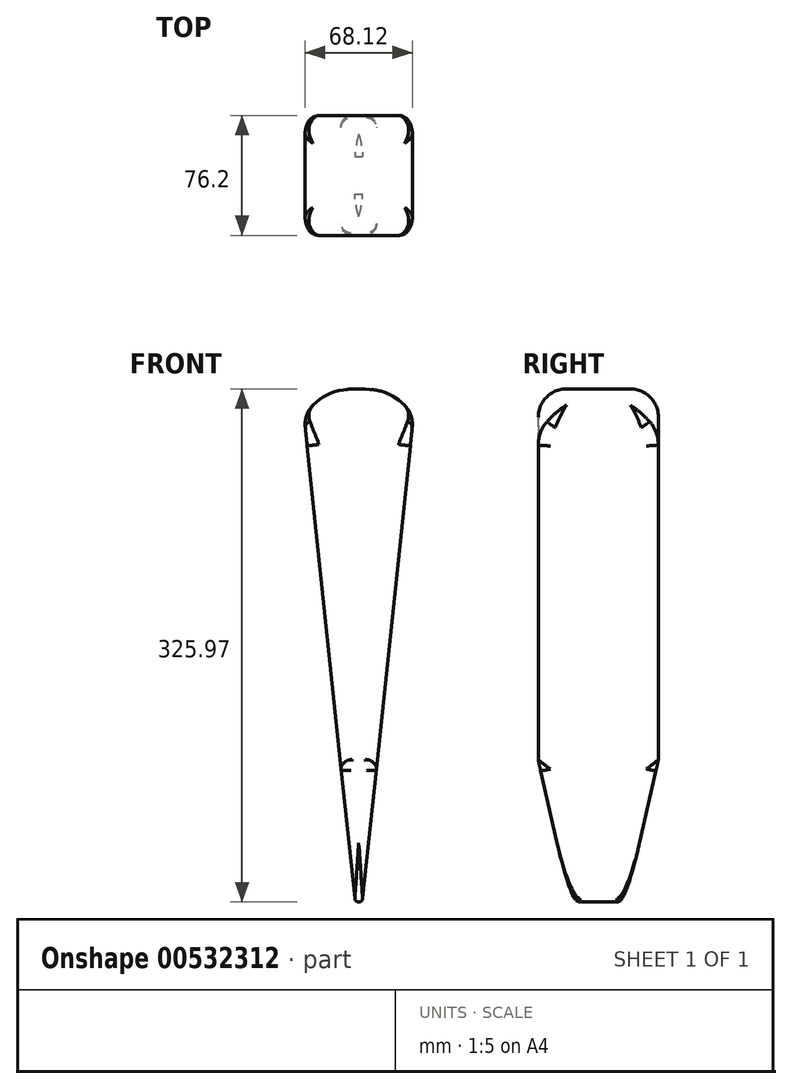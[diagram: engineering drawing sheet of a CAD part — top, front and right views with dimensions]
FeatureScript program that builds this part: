
annotation { "Feature Type Name" : "Feature", "Feature Type Description" : "" }
export const myFeature = defineFeature(function(context is Context, id is Id, definition is map)
    precondition{}
    {
        {
            var Q0;
            Q0=qCreatedBy(makeId("Front.planeOp"),FACE);
            var sketch = newSketch(context, id + "F0", { "sketchPlane" : qUnion([Q0])});
            skLineSegment(sketch, "E0", {"start": v(-58.84, 108.82) * mm, "end": v(-24.13, -221.38) * mm});
            skLineSegment(sketch, "E1", {"start": v(10.58, 108.82) * mm, "end": v(-24.13, -221.38) * mm});
            skLineSegment(sketch, "E2", {"start": v(-58.84, 108.82) * mm, "end": v(10.58, 108.82) * mm, "construction": true});
            skPoint(sketch, "E3", {"position": v(-24.13, 126.34) * mm});
            skFitSpline(sketch, "E4", {"points": [v(-58.84, 108.82) * mm, v(-24.13, 126.34) * mm, v(10.58, 108.82) * mm], "startDerivative": vector(63.45, 96.01) * mm, "endDerivative": vector(63.45, -96.01) * mm});
            skLineSegment(sketch, "E5", {"start": v(-58.84, 108.82) * mm, "end": v(-24.13, 126.34) * mm, "construction": true});
            skLineSegment(sketch, "E6", {"start": v(10.58, 108.82) * mm, "end": v(-24.13, 126.34) * mm, "construction": true});
            skLineSegment(sketch, "E7", {"start": v(-24.13, 126.34) * mm, "end": v(-24.13, 108.82) * mm, "construction": true});
            skLineSegment(sketch, "E8", {"start": v(-48.26, 124.82) * mm, "end": v(0, 124.82) * mm, "construction": true});
            skLineSegment(sketch, "E9", {"start": v(-58.84, 108.82) * mm, "end": v(-48.26, 124.82) * mm, "construction": true});
            skLineSegment(sketch, "E10", {"start": v(0, 124.82) * mm, "end": v(10.58, 108.82) * mm, "construction": true});
            skSolve(sketch);
        }
        {
            var Q0;
            Q0=makeQuery(id+"F0.imprint","IMPRINT",FACE,{"disambiguationData":[TD([[makeQuery(id+"F0.imprint","IMPRINT",EDGE,{"derivedFrom":sQuery(id+"F0.wireOp",EDGE,"E0")}),1.0]])]});
            extrude(context, id + "F1", {"entities" : qUnion([Q0]), "depth" : 76.2 * mm});
        }
        {
            var Q0;
            Q0=qCreatedBy(makeId("Right.planeOp"),FACE);
            var sketch = newSketch(context, id + "F2", { "sketchPlane" : qUnion([Q0])});
            skLineSegment(sketch, "E11", {"start": v(-255.45, -27.89) * mm, "end": v(-223.7, -167.59) * mm});
            skLineSegment(sketch, "E12", {"start": v(-223.7, -167.59) * mm, "end": v(-198.3, -167.59) * mm});
            skLineSegment(sketch, "E13", {"start": v(-198.3, -167.59) * mm, "end": v(-166.55, -27.89) * mm});
            skLineSegment(sketch, "E14", {"start": v(-162.92, -27.89) * mm, "end": v(-162.92, -186.53) * mm});
            skLineSegment(sketch, "E15", {"start": v(-162.92, -186.53) * mm, "end": v(-270.23, -186.53) * mm});
            skLineSegment(sketch, "E16", {"start": v(-270.23, -186.53) * mm, "end": v(-270.23, -27.89) * mm});
            skLineSegment(sketch, "E17", {"start": v(-270.23, -27.89) * mm, "end": v(-255.45, -27.89) * mm});
            skLineSegment(sketch, "E18", {"start": v(-166.55, -27.89) * mm, "end": v(-162.92, -27.89) * mm});
            skSolve(sketch);
        }
        {
            var Q0;
            Q0=makeQuery(id+"F2.imprint","IMPRINT",FACE,{"disambiguationData":[TD([[makeQuery(id+"F2.imprint","IMPRINT",EDGE,{"derivedFrom":sQuery(id+"F2.wireOp",EDGE,"E11")}),-1.0]])]});
            extrude(context, id + "F3", {"entities" : qUnion([Q0]), "depth" : 127 * mm, "symmetric" : true});
        }
        {
            var Q0;
            Q0=sQuery(id+"F2.wireOp",EDGE,"E12");
            cPoint(context, id + "F4", {"entities" : qUnion([Q0]), "parameter" : 0.5});
        }
        {
            var Q0;
            Q0=makeQuery(id+"F1.opExtrude","SWEPT_EDGE",EDGE,{"disambiguationData":[OSD([sQuery(id+"F0.wireOp",EDGE,"E0"),sQuery(id+"F0.wireOp",EDGE,"E1")])]});
            cPoint(context, id + "F5", {"entities" : qUnion([Q0]), "parameter" : 0.5});
        }
        {
            var Q0;
            Q0=makeQuery(id+"F3.opExtrude","SWEPT_BODY",BODY,{"disambiguationData":[OSD([sQuery(id+"F2.wireOp",EDGE,"E11"),sQuery(id+"F2.wireOp",EDGE,"E12"),sQuery(id+"F2.wireOp",EDGE,"E13"),sQuery(id+"F2.wireOp",EDGE,"E14"),sQuery(id+"F2.wireOp",EDGE,"E15"),sQuery(id+"F2.wireOp",EDGE,"E16"),sQuery(id+"F2.wireOp",EDGE,"E17"),sQuery(id+"F2.wireOp",EDGE,"E18")])]});
            var Q1;
            Q1=qCreatedBy(id+"F4",VERTEX);
            var Q2;
            Q2=qCreatedBy(id+"F5",VERTEX);
            transform(context, id + "F6", {"entities" : qUnion([Q0]), "transformType" : TransformType.TRANSLATION_ENTITY, "oppositeDirectionEntity" : false, "transformLine" : qUnion([Q1, Q2]), "makeCopy" : false});
        }
        {
            var Q0;
            Q0=makeQuery(id+"F3.opExtrude","SWEPT_BODY",BODY,{"disambiguationData":[OSD([sQuery(id+"F2.wireOp",EDGE,"E11"),sQuery(id+"F2.wireOp",EDGE,"E12"),sQuery(id+"F2.wireOp",EDGE,"E13"),sQuery(id+"F2.wireOp",EDGE,"E14"),sQuery(id+"F2.wireOp",EDGE,"E15"),sQuery(id+"F2.wireOp",EDGE,"E16"),sQuery(id+"F2.wireOp",EDGE,"E17"),sQuery(id+"F2.wireOp",EDGE,"E18")])]});
            var Q1;
            Q1=makeQuery(id+"F1.opExtrude","SWEPT_BODY",BODY,{"disambiguationData":[OSD([sQuery(id+"F0.wireOp",EDGE,"E0"),sQuery(id+"F0.wireOp",EDGE,"E1"),sQuery(id+"F0.wireOp",EDGE,"E4")])]});
            booleanBodies(context, id + "F7", {"operationType" : BooleanOperationType.SUBTRACTION, "tools" : qUnion([Q0]), "targets" : qUnion([Q1])});
        }
        {
            var Q0;
            Q0=makeQuery(id+"F1.opExtrude","CAP_EDGE",EDGE,{"disambiguationData":[OSD([sQuery(id+"F0.wireOp",EDGE,"E0")])],"isStart":false});
            fillet(context, id + "F8", {"entities" : qUnion([Q0]), "radius" : 7.62 * mm, "tangentPropagation" : true, "allowEdgeOverflow" : false});
        }
        {
            var Q0;
            Q0=makeQuery(id+"F1.opExtrude","CAP_EDGE",EDGE,{"disambiguationData":[OSD([sQuery(id+"F0.wireOp",EDGE,"E1")])],"isStart":false});
            fillet(context, id + "F9", {"entities" : qUnion([Q0]), "radius" : 7.62 * mm, "tangentPropagation" : true, "allowEdgeOverflow" : false});
        }
        {
            var Q0;
            Q0=makeQuery(id+"F1.opExtrude","CAP_EDGE",EDGE,{"disambiguationData":[OSD([sQuery(id+"F0.wireOp",EDGE,"E1")])],"isStart":true});
            fillet(context, id + "F10", {"entities" : qUnion([Q0]), "radius" : 7.62 * mm, "tangentPropagation" : true, "allowEdgeOverflow" : false});
        }
        {
            var Q0;
            Q0=makeQuery(id+"F1.opExtrude","CAP_EDGE",EDGE,{"disambiguationData":[OSD([sQuery(id+"F0.wireOp",EDGE,"E0")])],"isStart":true});
            fillet(context, id + "F11", {"entities" : qUnion([Q0]), "radius" : 7.62 * mm, "tangentPropagation" : true, "allowEdgeOverflow" : false});
        }
        {
            var Q0;
            Q0=makeQuery(id+"F1.opExtrude","SWEPT_FACE",FACE,{"disambiguationData":[OSD([sQuery(id+"F0.wireOp",EDGE,"E4")])]});
            fillet(context, id + "F12", {"entities" : qUnion([Q0]), "radius" : 17.78 * mm, "tangentPropagation" : true, "allowEdgeOverflow" : false});
        }
        {
            var Q0;
            Q0=makeQuery(id+"F7.opBoolean","INTERSECT",EDGE,{"derivedFrom":[makeQuery(id+"F1.opExtrude","SWEPT_FACE",FACE,{"disambiguationData":[OSD([sQuery(id+"F0.wireOp",EDGE,"E1")])]}),makeQuery(id+"F3.opExtrude","SWEPT_FACE",FACE,{"disambiguationData":[OSD([sQuery(id+"F2.wireOp",EDGE,"E11")])]})]});
            var Q1;
            Q1=makeQuery(id+"F7.opBoolean","INTERSECT",EDGE,{"derivedFrom":[makeQuery(id+"F1.opExtrude","SWEPT_FACE",FACE,{"disambiguationData":[OSD([sQuery(id+"F0.wireOp",EDGE,"E0")])]}),makeQuery(id+"F3.opExtrude","SWEPT_FACE",FACE,{"disambiguationData":[OSD([sQuery(id+"F2.wireOp",EDGE,"E11")])]})]});
            var Q2;
            Q2=makeQuery(id+"F7.opBoolean","INTERSECT",EDGE,{"derivedFrom":[makeQuery(id+"F1.opExtrude","SWEPT_FACE",FACE,{"disambiguationData":[OSD([sQuery(id+"F0.wireOp",EDGE,"E0")])]}),makeQuery(id+"F3.opExtrude","SWEPT_FACE",FACE,{"disambiguationData":[OSD([sQuery(id+"F2.wireOp",EDGE,"E13")])]})]});
            var Q3;
            Q3=makeQuery(id+"F7.opBoolean","INTERSECT",EDGE,{"derivedFrom":[makeQuery(id+"F1.opExtrude","SWEPT_FACE",FACE,{"disambiguationData":[OSD([sQuery(id+"F0.wireOp",EDGE,"E1")])]}),makeQuery(id+"F3.opExtrude","SWEPT_FACE",FACE,{"disambiguationData":[OSD([sQuery(id+"F2.wireOp",EDGE,"E13")])]})]});
            fillet(context, id + "F13", {"entities" : qUnion([Q0, Q1, Q2, Q3]), "radius" : 6.35 * mm, "tangentPropagation" : true, "allowEdgeOverflow" : false});
        }
        {
            var Q0;
            Q0=makeQuery(id+"F1.opExtrude","SWEPT_EDGE",EDGE,{"disambiguationData":[OSD([sQuery(id+"F0.wireOp",EDGE,"E0"),sQuery(id+"F0.wireOp",EDGE,"E1")])]});
            fillet(context, id + "F14", {"entities" : qUnion([Q0]), "radius" : 2.54 * mm, "tangentPropagation" : true, "allowEdgeOverflow" : false});
        }
    });
